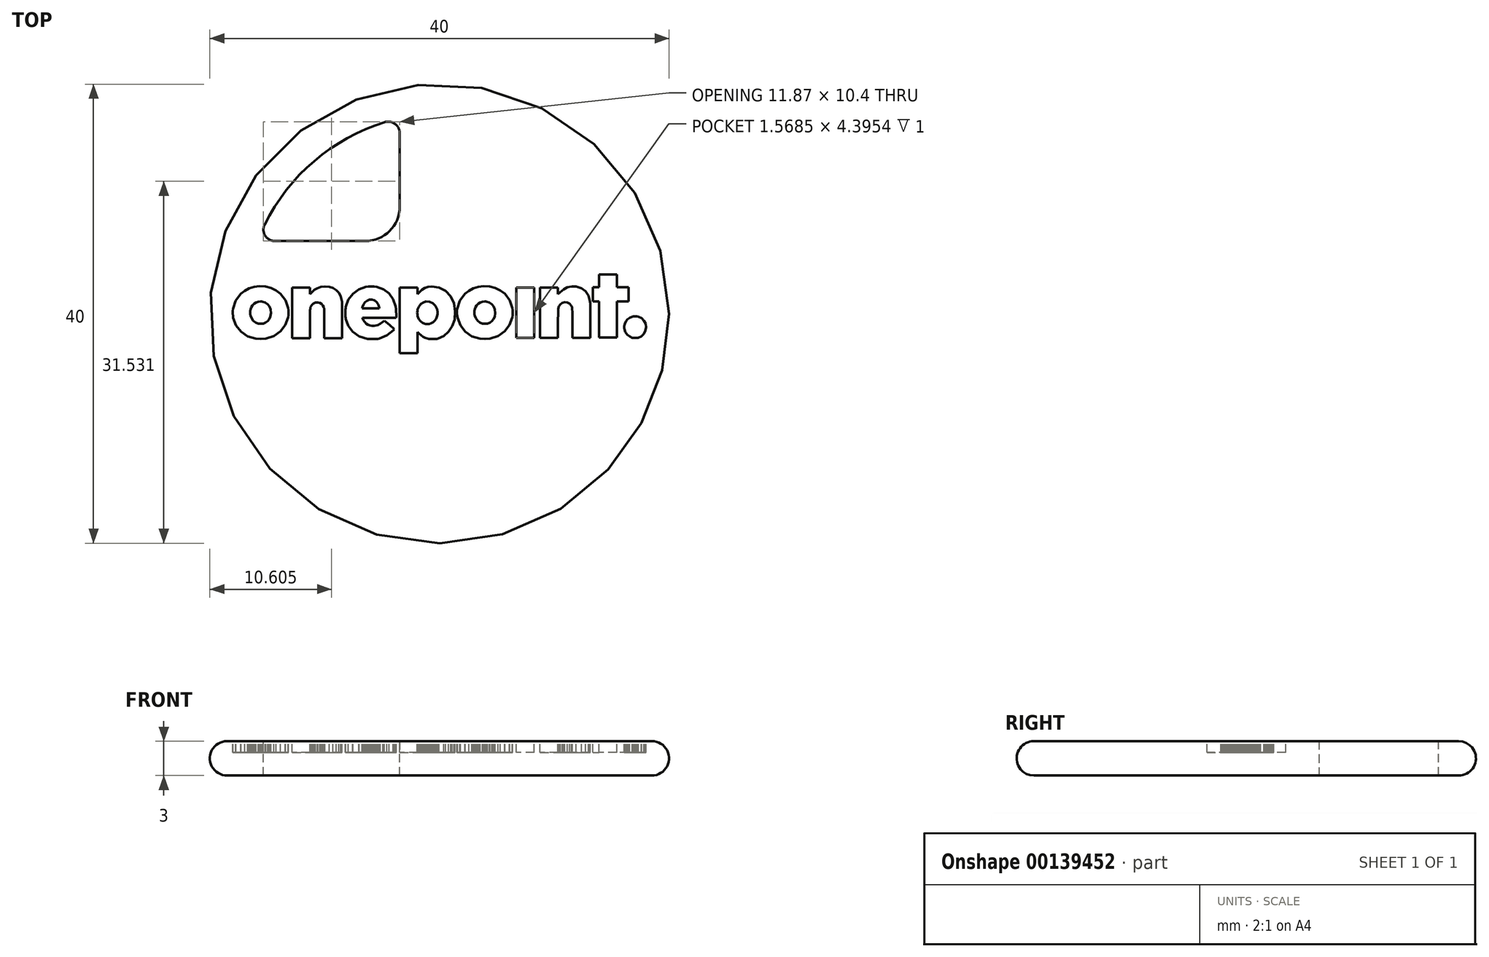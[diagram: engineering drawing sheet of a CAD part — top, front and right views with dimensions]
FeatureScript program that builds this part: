
annotation { "Feature Type Name" : "Feature", "Feature Type Description" : "" }
export const myFeature = defineFeature(function(context is Context, id is Id, definition is map)
    precondition{}
    {
        {
            var Q0;
            Q0=qCreatedBy(makeId("Top.planeOp"),FACE);
            var sketch = newSketch(context, id + "F0", { "sketchPlane" : qUnion([Q0])});
            skCircle(sketch, "E0", {"center": v(0, 0) * mm, "radius": 20 * mm});
            skSolve(sketch);
        }
        {
            var Q0;
            Q0 = qSketchRegion(id + "F0", true);
            var Q1;
            Q1=sQuery(id+"F0.wireOp",EDGE,"E0");
            extrude(context, id + "F1", {"entities" : qUnion([Q0]), "surfaceEntities" : qUnion([Q1]), "depth" : 3 * mm});
        }
        {
            var Q0;
            Q0=makeQuery(id+"F1.opExtrude","CAP_FACE",FACE,{"disambiguationData":[OSD([sQuery(id+"F0.wireOp",EDGE,"E0")])],"isStart":false});
            var sketch = newSketch(context, id + "F2", { "sketchPlane" : qUnion([Q0])});
            skLineSegment(sketch, "E1", {"start": v(-16, -2.18) * mm, "end": v(-16.7, -1.96) * mm});
            skLineSegment(sketch, "E2", {"start": v(-16.7, -1.96) * mm, "end": v(-17.28, -1.58) * mm});
            skLineSegment(sketch, "E3", {"start": v(-17.28, -1.58) * mm, "end": v(-17.7, -1.04) * mm});
            skLineSegment(sketch, "E4", {"start": v(-17.7, -1.04) * mm, "end": v(-17.96, -0.37) * mm});
            skLineSegment(sketch, "E5", {"start": v(-17.96, -0.37) * mm, "end": v(-17.99, -0.2) * mm});
            skLineSegment(sketch, "E6", {"start": v(-17.99, -0.2) * mm, "end": v(-18, 0.02) * mm});
            skLineSegment(sketch, "E7", {"start": v(-18, 0.02) * mm, "end": v(-18, 0.24) * mm});
            skLineSegment(sketch, "E8", {"start": v(-18, 0.24) * mm, "end": v(-17.98, 0.43) * mm});
            skLineSegment(sketch, "E9", {"start": v(-17.98, 0.43) * mm, "end": v(-17.75, 1.13) * mm});
            skLineSegment(sketch, "E10", {"start": v(-17.75, 1.13) * mm, "end": v(-17.3, 1.72) * mm});
            skLineSegment(sketch, "E11", {"start": v(-17.3, 1.72) * mm, "end": v(-16.96, 2) * mm});
            skLineSegment(sketch, "E12", {"start": v(-16.96, 2) * mm, "end": v(-16.57, 2.2) * mm});
            skLineSegment(sketch, "E13", {"start": v(-16.57, 2.2) * mm, "end": v(-16.15, 2.33) * mm});
            skLineSegment(sketch, "E14", {"start": v(-16.15, 2.33) * mm, "end": v(-15.69, 2.4) * mm});
            skLineSegment(sketch, "E15", {"start": v(-15.69, 2.4) * mm, "end": v(-15.16, 2.37) * mm});
            skLineSegment(sketch, "E16", {"start": v(-15.16, 2.37) * mm, "end": v(-14.67, 2.24) * mm});
            skLineSegment(sketch, "E17", {"start": v(-14.67, 2.24) * mm, "end": v(-14.22, 2.03) * mm});
            skLineSegment(sketch, "E18", {"start": v(-14.22, 2.03) * mm, "end": v(-13.83, 1.72) * mm});
            skLineSegment(sketch, "E19", {"start": v(-13.83, 1.72) * mm, "end": v(-13.4, 1.16) * mm});
            skLineSegment(sketch, "E20", {"start": v(-13.4, 1.16) * mm, "end": v(-13.17, 0.5) * mm});
            skLineSegment(sketch, "E21", {"start": v(-13.17, 0.5) * mm, "end": v(-13.15, 0.3) * mm});
            skLineSegment(sketch, "E22", {"start": v(-13.15, 0.3) * mm, "end": v(-13.15, 0.09) * mm});
            skLineSegment(sketch, "E23", {"start": v(-13.15, 0.09) * mm, "end": v(-13.16, -0.13) * mm});
            skLineSegment(sketch, "E24", {"start": v(-13.16, -0.13) * mm, "end": v(-13.18, -0.32) * mm});
            skLineSegment(sketch, "E25", {"start": v(-13.18, -0.32) * mm, "end": v(-13.42, -1) * mm});
            skLineSegment(sketch, "E26", {"start": v(-13.42, -1) * mm, "end": v(-13.85, -1.54) * mm});
            skLineSegment(sketch, "E27", {"start": v(-13.85, -1.54) * mm, "end": v(-14.43, -1.94) * mm});
            skLineSegment(sketch, "E28", {"start": v(-14.43, -1.94) * mm, "end": v(-15.12, -2.17) * mm});
            skLineSegment(sketch, "E29", {"start": v(-15.12, -2.17) * mm, "end": v(-15.56, -2.2) * mm});
            skLineSegment(sketch, "E30", {"start": v(-15.56, -2.2) * mm, "end": v(-16, -2.18) * mm});
            skLineSegment(sketch, "E31", {"start": v(-16, -2.18) * mm, "end": v(-16, -2.18) * mm});
            skLineSegment(sketch, "E32", {"start": v(-15.34, -0.86) * mm, "end": v(-15.13, -0.77) * mm});
            skLineSegment(sketch, "E33", {"start": v(-15.13, -0.77) * mm, "end": v(-14.96, -0.65) * mm});
            skLineSegment(sketch, "E34", {"start": v(-14.96, -0.65) * mm, "end": v(-14.82, -0.47) * mm});
            skLineSegment(sketch, "E35", {"start": v(-14.82, -0.47) * mm, "end": v(-14.72, -0.26) * mm});
            skLineSegment(sketch, "E36", {"start": v(-14.72, -0.26) * mm, "end": v(-14.66, 0.07) * mm});
            skLineSegment(sketch, "E37", {"start": v(-14.66, 0.07) * mm, "end": v(-14.7, 0.38) * mm});
            skLineSegment(sketch, "E38", {"start": v(-14.7, 0.38) * mm, "end": v(-14.8, 0.62) * mm});
            skLineSegment(sketch, "E39", {"start": v(-14.8, 0.62) * mm, "end": v(-14.97, 0.82) * mm});
            skLineSegment(sketch, "E40", {"start": v(-14.97, 0.82) * mm, "end": v(-15.17, 0.97) * mm});
            skLineSegment(sketch, "E41", {"start": v(-15.17, 0.97) * mm, "end": v(-15.41, 1.05) * mm});
            skLineSegment(sketch, "E42", {"start": v(-15.41, 1.05) * mm, "end": v(-15.51, 1.08) * mm});
            skLineSegment(sketch, "E43", {"start": v(-15.51, 1.08) * mm, "end": v(-15.59, 1.08) * mm});
            skLineSegment(sketch, "E44", {"start": v(-15.59, 1.08) * mm, "end": v(-15.78, 1.05) * mm});
            skLineSegment(sketch, "E45", {"start": v(-15.78, 1.05) * mm, "end": v(-15.99, 0.98) * mm});
            skLineSegment(sketch, "E46", {"start": v(-15.99, 0.98) * mm, "end": v(-16.15, 0.87) * mm});
            skLineSegment(sketch, "E47", {"start": v(-16.15, 0.87) * mm, "end": v(-16.28, 0.73) * mm});
            skLineSegment(sketch, "E48", {"start": v(-16.28, 0.73) * mm, "end": v(-16.39, 0.56) * mm});
            skLineSegment(sketch, "E49", {"start": v(-16.39, 0.56) * mm, "end": v(-16.45, 0.37) * mm});
            skLineSegment(sketch, "E50", {"start": v(-16.45, 0.37) * mm, "end": v(-16.48, 0.25) * mm});
            skLineSegment(sketch, "E51", {"start": v(-16.48, 0.25) * mm, "end": v(-16.48, 0.1) * mm});
            skLineSegment(sketch, "E52", {"start": v(-16.48, 0.1) * mm, "end": v(-16.48, -0.04) * mm});
            skLineSegment(sketch, "E53", {"start": v(-16.48, -0.04) * mm, "end": v(-16.45, -0.15) * mm});
            skLineSegment(sketch, "E54", {"start": v(-16.45, -0.15) * mm, "end": v(-16.36, -0.4) * mm});
            skLineSegment(sketch, "E55", {"start": v(-16.36, -0.4) * mm, "end": v(-16.21, -0.6) * mm});
            skLineSegment(sketch, "E56", {"start": v(-16.21, -0.6) * mm, "end": v(-16.02, -0.76) * mm});
            skLineSegment(sketch, "E57", {"start": v(-16.02, -0.76) * mm, "end": v(-15.8, -0.86) * mm});
            skLineSegment(sketch, "E58", {"start": v(-15.8, -0.86) * mm, "end": v(-15.57, -0.88) * mm});
            skLineSegment(sketch, "E59", {"start": v(-15.57, -0.88) * mm, "end": v(-15.34, -0.86) * mm});
            skLineSegment(sketch, "E60", {"start": v(-15.34, -0.86) * mm, "end": v(-15.34, -0.86) * mm});
            skLineSegment(sketch, "E61", {"start": v(-12.83, 0.07) * mm, "end": v(-12.83, 2.27) * mm});
            skLineSegment(sketch, "E62", {"start": v(-12.83, 2.27) * mm, "end": v(-11.27, 2.27) * mm});
            skLineSegment(sketch, "E63", {"start": v(-11.27, 2.27) * mm, "end": v(-11.27, 1.7) * mm});
            skLineSegment(sketch, "E64", {"start": v(-11.27, 1.7) * mm, "end": v(-11.1, 1.87) * mm});
            skLineSegment(sketch, "E65", {"start": v(-11.1, 1.87) * mm, "end": v(-10.88, 2.08) * mm});
            skLineSegment(sketch, "E66", {"start": v(-10.88, 2.08) * mm, "end": v(-10.63, 2.22) * mm});
            skLineSegment(sketch, "E67", {"start": v(-10.63, 2.22) * mm, "end": v(-10.31, 2.33) * mm});
            skLineSegment(sketch, "E68", {"start": v(-10.31, 2.33) * mm, "end": v(-9.96, 2.37) * mm});
            skLineSegment(sketch, "E69", {"start": v(-9.96, 2.37) * mm, "end": v(-9.6, 2.34) * mm});
            skLineSegment(sketch, "E70", {"start": v(-9.6, 2.34) * mm, "end": v(-9.27, 2.23) * mm});
            skLineSegment(sketch, "E71", {"start": v(-9.27, 2.23) * mm, "end": v(-9, 2.06) * mm});
            skLineSegment(sketch, "E72", {"start": v(-9, 2.06) * mm, "end": v(-8.78, 1.83) * mm});
            skLineSegment(sketch, "E73", {"start": v(-8.78, 1.83) * mm, "end": v(-8.62, 1.54) * mm});
            skLineSegment(sketch, "E74", {"start": v(-8.62, 1.54) * mm, "end": v(-8.5, 1.18) * mm});
            skLineSegment(sketch, "E75", {"start": v(-8.5, 1.18) * mm, "end": v(-8.5, 1.13) * mm});
            skLineSegment(sketch, "E76", {"start": v(-8.5, 1.13) * mm, "end": v(-8.49, 1.06) * mm});
            skLineSegment(sketch, "E77", {"start": v(-8.49, 1.06) * mm, "end": v(-8.48, 0.95) * mm});
            skLineSegment(sketch, "E78", {"start": v(-8.48, 0.95) * mm, "end": v(-8.48, 0.8) * mm});
            skLineSegment(sketch, "E79", {"start": v(-8.48, 0.8) * mm, "end": v(-8.48, 0.59) * mm});
            skLineSegment(sketch, "E80", {"start": v(-8.48, 0.59) * mm, "end": v(-8.47, 0.3) * mm});
            skLineSegment(sketch, "E81", {"start": v(-8.47, 0.3) * mm, "end": v(-8.47, -0.07) * mm});
            skLineSegment(sketch, "E82", {"start": v(-8.47, -0.07) * mm, "end": v(-8.47, -0.54) * mm});
            skLineSegment(sketch, "E83", {"start": v(-8.47, -0.54) * mm, "end": v(-8.47, -2.13) * mm});
            skLineSegment(sketch, "E84", {"start": v(-8.47, -2.13) * mm, "end": v(-10.02, -2.13) * mm});
            skLineSegment(sketch, "E85", {"start": v(-10.02, -2.13) * mm, "end": v(-10.02, -0.85) * mm});
            skLineSegment(sketch, "E86", {"start": v(-10.02, -0.85) * mm, "end": v(-10.03, -0.43) * mm});
            skLineSegment(sketch, "E87", {"start": v(-10.03, -0.43) * mm, "end": v(-10.03, -0.1) * mm});
            skLineSegment(sketch, "E88", {"start": v(-10.03, -0.1) * mm, "end": v(-10.03, 0.13) * mm});
            skLineSegment(sketch, "E89", {"start": v(-10.03, 0.13) * mm, "end": v(-10.04, 0.29) * mm});
            skLineSegment(sketch, "E90", {"start": v(-10.04, 0.29) * mm, "end": v(-10.04, 0.4) * mm});
            skLineSegment(sketch, "E91", {"start": v(-10.04, 0.4) * mm, "end": v(-10.05, 0.46) * mm});
            skLineSegment(sketch, "E92", {"start": v(-10.05, 0.46) * mm, "end": v(-10.06, 0.5) * mm});
            skLineSegment(sketch, "E93", {"start": v(-10.06, 0.5) * mm, "end": v(-10.07, 0.55) * mm});
            skLineSegment(sketch, "E94", {"start": v(-10.07, 0.55) * mm, "end": v(-10.15, 0.72) * mm});
            skLineSegment(sketch, "E95", {"start": v(-10.15, 0.72) * mm, "end": v(-10.26, 0.86) * mm});
            skLineSegment(sketch, "E96", {"start": v(-10.26, 0.86) * mm, "end": v(-10.4, 0.94) * mm});
            skLineSegment(sketch, "E97", {"start": v(-10.4, 0.94) * mm, "end": v(-10.58, 0.98) * mm});
            skLineSegment(sketch, "E98", {"start": v(-10.58, 0.98) * mm, "end": v(-10.8, 0.97) * mm});
            skLineSegment(sketch, "E99", {"start": v(-10.8, 0.97) * mm, "end": v(-10.97, 0.89) * mm});
            skLineSegment(sketch, "E100", {"start": v(-10.97, 0.89) * mm, "end": v(-11.12, 0.75) * mm});
            skLineSegment(sketch, "E101", {"start": v(-11.12, 0.75) * mm, "end": v(-11.23, 0.57) * mm});
            skLineSegment(sketch, "E102", {"start": v(-11.23, 0.57) * mm, "end": v(-11.24, 0.53) * mm});
            skLineSegment(sketch, "E103", {"start": v(-11.24, 0.53) * mm, "end": v(-11.25, 0.5) * mm});
            skLineSegment(sketch, "E104", {"start": v(-11.25, 0.5) * mm, "end": v(-11.26, 0.42) * mm});
            skLineSegment(sketch, "E105", {"start": v(-11.26, 0.42) * mm, "end": v(-11.26, 0.32) * mm});
            skLineSegment(sketch, "E106", {"start": v(-11.26, 0.32) * mm, "end": v(-11.26, 0.15) * mm});
            skLineSegment(sketch, "E107", {"start": v(-11.26, 0.15) * mm, "end": v(-11.27, -0.08) * mm});
            skLineSegment(sketch, "E108", {"start": v(-11.27, -0.08) * mm, "end": v(-11.27, -0.4) * mm});
            skLineSegment(sketch, "E109", {"start": v(-11.27, -0.4) * mm, "end": v(-11.27, -0.83) * mm});
            skLineSegment(sketch, "E110", {"start": v(-11.27, -0.83) * mm, "end": v(-11.27, -2.13) * mm});
            skLineSegment(sketch, "E111", {"start": v(-11.27, -2.13) * mm, "end": v(-12.83, -2.13) * mm});
            skLineSegment(sketch, "E112", {"start": v(-12.83, -2.13) * mm, "end": v(-12.83, 0.07) * mm});
            skLineSegment(sketch, "E113", {"start": v(-12.83, 0.07) * mm, "end": v(-12.83, 0.07) * mm});
            skLineSegment(sketch, "E114", {"start": v(-6.25, -2.2) * mm, "end": v(-6.98, -1.98) * mm});
            skLineSegment(sketch, "E115", {"start": v(-6.98, -1.98) * mm, "end": v(-7.57, -1.56) * mm});
            skLineSegment(sketch, "E116", {"start": v(-7.57, -1.56) * mm, "end": v(-7.94, -1.06) * mm});
            skLineSegment(sketch, "E117", {"start": v(-7.94, -1.06) * mm, "end": v(-8.16, -0.45) * mm});
            skLineSegment(sketch, "E118", {"start": v(-8.16, -0.45) * mm, "end": v(-8.18, -0.35) * mm});
            skLineSegment(sketch, "E119", {"start": v(-8.18, -0.35) * mm, "end": v(-8.19, -0.25) * mm});
            skLineSegment(sketch, "E120", {"start": v(-8.19, -0.25) * mm, "end": v(-8.2, -0.12) * mm});
            skLineSegment(sketch, "E121", {"start": v(-8.2, -0.12) * mm, "end": v(-8.2, 0.06) * mm});
            skLineSegment(sketch, "E122", {"start": v(-8.2, 0.06) * mm, "end": v(-8.2, 0.25) * mm});
            skLineSegment(sketch, "E123", {"start": v(-8.2, 0.25) * mm, "end": v(-8.19, 0.38) * mm});
            skLineSegment(sketch, "E124", {"start": v(-8.19, 0.38) * mm, "end": v(-8.18, 0.48) * mm});
            skLineSegment(sketch, "E125", {"start": v(-8.18, 0.48) * mm, "end": v(-8.16, 0.58) * mm});
            skLineSegment(sketch, "E126", {"start": v(-8.16, 0.58) * mm, "end": v(-7.93, 1.22) * mm});
            skLineSegment(sketch, "E127", {"start": v(-7.93, 1.22) * mm, "end": v(-7.54, 1.74) * mm});
            skLineSegment(sketch, "E128", {"start": v(-7.54, 1.74) * mm, "end": v(-7.03, 2.13) * mm});
            skLineSegment(sketch, "E129", {"start": v(-7.03, 2.13) * mm, "end": v(-6.41, 2.34) * mm});
            skLineSegment(sketch, "E130", {"start": v(-6.41, 2.34) * mm, "end": v(-6.2, 2.37) * mm});
            skLineSegment(sketch, "E131", {"start": v(-6.2, 2.37) * mm, "end": v(-5.95, 2.37) * mm});
            skLineSegment(sketch, "E132", {"start": v(-5.95, 2.37) * mm, "end": v(-5.69, 2.36) * mm});
            skLineSegment(sketch, "E133", {"start": v(-5.69, 2.36) * mm, "end": v(-5.47, 2.33) * mm});
            skLineSegment(sketch, "E134", {"start": v(-5.47, 2.33) * mm, "end": v(-4.87, 2.12) * mm});
            skLineSegment(sketch, "E135", {"start": v(-4.87, 2.12) * mm, "end": v(-4.4, 1.75) * mm});
            skLineSegment(sketch, "E136", {"start": v(-4.4, 1.75) * mm, "end": v(-4.04, 1.25) * mm});
            skLineSegment(sketch, "E137", {"start": v(-4.04, 1.25) * mm, "end": v(-3.82, 0.6) * mm});
            skLineSegment(sketch, "E138", {"start": v(-3.82, 0.6) * mm, "end": v(-3.8, 0.41) * mm});
            skLineSegment(sketch, "E139", {"start": v(-3.8, 0.41) * mm, "end": v(-3.77, 0.17) * mm});
            skLineSegment(sketch, "E140", {"start": v(-3.77, 0.17) * mm, "end": v(-3.76, -0.06) * mm});
            skLineSegment(sketch, "E141", {"start": v(-3.76, -0.06) * mm, "end": v(-3.76, -0.23) * mm});
            skLineSegment(sketch, "E142", {"start": v(-3.76, -0.23) * mm, "end": v(-3.78, -0.36) * mm});
            skLineSegment(sketch, "E143", {"start": v(-3.78, -0.36) * mm, "end": v(-6.7, -0.36) * mm});
            skLineSegment(sketch, "E144", {"start": v(-6.7, -0.36) * mm, "end": v(-6.7, -0.4) * mm});
            skLineSegment(sketch, "E145", {"start": v(-6.7, -0.4) * mm, "end": v(-6.67, -0.46) * mm});
            skLineSegment(sketch, "E146", {"start": v(-6.67, -0.46) * mm, "end": v(-6.63, -0.56) * mm});
            skLineSegment(sketch, "E147", {"start": v(-6.63, -0.56) * mm, "end": v(-6.52, -0.72) * mm});
            skLineSegment(sketch, "E148", {"start": v(-6.52, -0.72) * mm, "end": v(-6.39, -0.86) * mm});
            skLineSegment(sketch, "E149", {"start": v(-6.39, -0.86) * mm, "end": v(-6.22, -0.96) * mm});
            skLineSegment(sketch, "E150", {"start": v(-6.22, -0.96) * mm, "end": v(-6.03, -1.03) * mm});
            skLineSegment(sketch, "E151", {"start": v(-6.03, -1.03) * mm, "end": v(-5.88, -1.05) * mm});
            skLineSegment(sketch, "E152", {"start": v(-5.88, -1.05) * mm, "end": v(-5.7, -1.05) * mm});
            skLineSegment(sketch, "E153", {"start": v(-5.7, -1.05) * mm, "end": v(-5.53, -1.03) * mm});
            skLineSegment(sketch, "E154", {"start": v(-5.53, -1.03) * mm, "end": v(-5.38, -1) * mm});
            skLineSegment(sketch, "E155", {"start": v(-5.38, -1) * mm, "end": v(-5.15, -0.88) * mm});
            skLineSegment(sketch, "E156", {"start": v(-5.15, -0.88) * mm, "end": v(-4.92, -0.71) * mm});
            skLineSegment(sketch, "E157", {"start": v(-4.92, -0.71) * mm, "end": v(-4.8, -0.6) * mm});
            skLineSegment(sketch, "E158", {"start": v(-4.8, -0.6) * mm, "end": v(-4.36, -0.97) * mm});
            skLineSegment(sketch, "E159", {"start": v(-4.36, -0.97) * mm, "end": v(-3.93, -1.33) * mm});
            skLineSegment(sketch, "E160", {"start": v(-3.93, -1.33) * mm, "end": v(-4, -1.42) * mm});
            skLineSegment(sketch, "E161", {"start": v(-4, -1.42) * mm, "end": v(-4.56, -1.9) * mm});
            skLineSegment(sketch, "E162", {"start": v(-4.56, -1.9) * mm, "end": v(-5.25, -2.17) * mm});
            skLineSegment(sketch, "E163", {"start": v(-5.25, -2.17) * mm, "end": v(-5.35, -2.19) * mm});
            skLineSegment(sketch, "E164", {"start": v(-5.35, -2.19) * mm, "end": v(-5.46, -2.2) * mm});
            skLineSegment(sketch, "E165", {"start": v(-5.46, -2.2) * mm, "end": v(-5.6, -2.2) * mm});
            skLineSegment(sketch, "E166", {"start": v(-5.6, -2.2) * mm, "end": v(-5.8, -2.2) * mm});
            skLineSegment(sketch, "E167", {"start": v(-5.8, -2.2) * mm, "end": v(-5.94, -2.21) * mm});
            skLineSegment(sketch, "E168", {"start": v(-5.94, -2.21) * mm, "end": v(-6.07, -2.21) * mm});
            skLineSegment(sketch, "E169", {"start": v(-6.07, -2.21) * mm, "end": v(-6.18, -2.2) * mm});
            skLineSegment(sketch, "E170", {"start": v(-6.18, -2.2) * mm, "end": v(-6.25, -2.2) * mm});
            skLineSegment(sketch, "E171", {"start": v(-6.25, -2.2) * mm, "end": v(-6.25, -2.2) * mm});
            skLineSegment(sketch, "E172", {"start": v(-5.23, 0.47) * mm, "end": v(-5.24, 0.54) * mm});
            skLineSegment(sketch, "E173", {"start": v(-5.24, 0.54) * mm, "end": v(-5.26, 0.63) * mm});
            skLineSegment(sketch, "E174", {"start": v(-5.26, 0.63) * mm, "end": v(-5.3, 0.74) * mm});
            skLineSegment(sketch, "E175", {"start": v(-5.3, 0.74) * mm, "end": v(-5.34, 0.83) * mm});
            skLineSegment(sketch, "E176", {"start": v(-5.34, 0.83) * mm, "end": v(-5.47, 1.02) * mm});
            skLineSegment(sketch, "E177", {"start": v(-5.47, 1.02) * mm, "end": v(-5.65, 1.15) * mm});
            skLineSegment(sketch, "E178", {"start": v(-5.65, 1.15) * mm, "end": v(-5.86, 1.22) * mm});
            skLineSegment(sketch, "E179", {"start": v(-5.86, 1.22) * mm, "end": v(-6.1, 1.22) * mm});
            skLineSegment(sketch, "E180", {"start": v(-6.1, 1.22) * mm, "end": v(-6.3, 1.14) * mm});
            skLineSegment(sketch, "E181", {"start": v(-6.3, 1.14) * mm, "end": v(-6.47, 1) * mm});
            skLineSegment(sketch, "E182", {"start": v(-6.47, 1) * mm, "end": v(-6.6, 0.82) * mm});
            skLineSegment(sketch, "E183", {"start": v(-6.6, 0.82) * mm, "end": v(-6.7, 0.58) * mm});
            skLineSegment(sketch, "E184", {"start": v(-6.7, 0.58) * mm, "end": v(-6.73, 0.45) * mm});
            skLineSegment(sketch, "E185", {"start": v(-6.73, 0.45) * mm, "end": v(-5.98, 0.45) * mm});
            skLineSegment(sketch, "E186", {"start": v(-5.98, 0.45) * mm, "end": v(-5.75, 0.45) * mm});
            skLineSegment(sketch, "E187", {"start": v(-5.75, 0.45) * mm, "end": v(-5.57, 0.45) * mm});
            skLineSegment(sketch, "E188", {"start": v(-5.57, 0.45) * mm, "end": v(-5.44, 0.46) * mm});
            skLineSegment(sketch, "E189", {"start": v(-5.44, 0.46) * mm, "end": v(-5.35, 0.46) * mm});
            skLineSegment(sketch, "E190", {"start": v(-5.35, 0.46) * mm, "end": v(-5.29, 0.46) * mm});
            skLineSegment(sketch, "E191", {"start": v(-5.29, 0.46) * mm, "end": v(-5.25, 0.46) * mm});
            skLineSegment(sketch, "E192", {"start": v(-5.25, 0.46) * mm, "end": v(-5.23, 0.47) * mm});
            skLineSegment(sketch, "E193", {"start": v(-5.23, 0.47) * mm, "end": v(-5.23, 0.47) * mm});
            skLineSegment(sketch, "E194", {"start": v(-3.46, -0.57) * mm, "end": v(-3.46, 2.28) * mm});
            skLineSegment(sketch, "E195", {"start": v(-3.46, 2.28) * mm, "end": v(-1.9, 2.28) * mm});
            skLineSegment(sketch, "E196", {"start": v(-1.9, 2.28) * mm, "end": v(-1.9, 1.71) * mm});
            skLineSegment(sketch, "E197", {"start": v(-1.9, 1.71) * mm, "end": v(-1.76, 1.87) * mm});
            skLineSegment(sketch, "E198", {"start": v(-1.76, 1.87) * mm, "end": v(-1.51, 2.08) * mm});
            skLineSegment(sketch, "E199", {"start": v(-1.51, 2.08) * mm, "end": v(-1.26, 2.24) * mm});
            skLineSegment(sketch, "E200", {"start": v(-1.26, 2.24) * mm, "end": v(-0.98, 2.33) * mm});
            skLineSegment(sketch, "E201", {"start": v(-0.98, 2.33) * mm, "end": v(-0.67, 2.37) * mm});
            skLineSegment(sketch, "E202", {"start": v(-0.67, 2.37) * mm, "end": v(-0.03, 2.3) * mm});
            skLineSegment(sketch, "E203", {"start": v(-0.03, 2.3) * mm, "end": v(0.53, 2) * mm});
            skLineSegment(sketch, "E204", {"start": v(0.53, 2) * mm, "end": v(0.97, 1.53) * mm});
            skLineSegment(sketch, "E205", {"start": v(0.97, 1.53) * mm, "end": v(1.26, 0.9) * mm});
            skLineSegment(sketch, "E206", {"start": v(1.26, 0.9) * mm, "end": v(1.37, 0.2) * mm});
            skLineSegment(sketch, "E207", {"start": v(1.37, 0.2) * mm, "end": v(1.32, -0.53) * mm});
            skLineSegment(sketch, "E208", {"start": v(1.32, -0.53) * mm, "end": v(1.12, -1.1) * mm});
            skLineSegment(sketch, "E209", {"start": v(1.12, -1.1) * mm, "end": v(0.8, -1.58) * mm});
            skLineSegment(sketch, "E210", {"start": v(0.8, -1.58) * mm, "end": v(0.39, -1.94) * mm});
            skLineSegment(sketch, "E211", {"start": v(0.39, -1.94) * mm, "end": v(-0.12, -2.17) * mm});
            skLineSegment(sketch, "E212", {"start": v(-0.12, -2.17) * mm, "end": v(-0.22, -2.2) * mm});
            skLineSegment(sketch, "E213", {"start": v(-0.22, -2.2) * mm, "end": v(-0.31, -2.2) * mm});
            skLineSegment(sketch, "E214", {"start": v(-0.31, -2.2) * mm, "end": v(-0.42, -2.2) * mm});
            skLineSegment(sketch, "E215", {"start": v(-0.42, -2.2) * mm, "end": v(-0.57, -2.2) * mm});
            skLineSegment(sketch, "E216", {"start": v(-0.57, -2.2) * mm, "end": v(-0.73, -2.2) * mm});
            skLineSegment(sketch, "E217", {"start": v(-0.73, -2.2) * mm, "end": v(-0.84, -2.2) * mm});
            skLineSegment(sketch, "E218", {"start": v(-0.84, -2.2) * mm, "end": v(-0.93, -2.2) * mm});
            skLineSegment(sketch, "E219", {"start": v(-0.93, -2.2) * mm, "end": v(-1.03, -2.17) * mm});
            skLineSegment(sketch, "E220", {"start": v(-1.03, -2.17) * mm, "end": v(-1.23, -2.1) * mm});
            skLineSegment(sketch, "E221", {"start": v(-1.23, -2.1) * mm, "end": v(-1.42, -2) * mm});
            skLineSegment(sketch, "E222", {"start": v(-1.42, -2) * mm, "end": v(-1.6, -1.88) * mm});
            skLineSegment(sketch, "E223", {"start": v(-1.6, -1.88) * mm, "end": v(-1.78, -1.72) * mm});
            skLineSegment(sketch, "E224", {"start": v(-1.78, -1.72) * mm, "end": v(-1.9, -1.6) * mm});
            skLineSegment(sketch, "E225", {"start": v(-1.9, -1.6) * mm, "end": v(-1.9, -3.43) * mm});
            skLineSegment(sketch, "E226", {"start": v(-1.9, -3.43) * mm, "end": v(-3.46, -3.43) * mm});
            skLineSegment(sketch, "E227", {"start": v(-3.46, -3.43) * mm, "end": v(-3.46, -0.57) * mm});
            skLineSegment(sketch, "E228", {"start": v(-3.46, -0.57) * mm, "end": v(-3.46, -0.57) * mm});
            skLineSegment(sketch, "E229", {"start": v(-0.9, -0.9) * mm, "end": v(-0.72, -0.85) * mm});
            skLineSegment(sketch, "E230", {"start": v(-0.72, -0.85) * mm, "end": v(-0.55, -0.75) * mm});
            skLineSegment(sketch, "E231", {"start": v(-0.55, -0.75) * mm, "end": v(-0.4, -0.61) * mm});
            skLineSegment(sketch, "E232", {"start": v(-0.4, -0.61) * mm, "end": v(-0.28, -0.45) * mm});
            skLineSegment(sketch, "E233", {"start": v(-0.28, -0.45) * mm, "end": v(-0.2, -0.26) * mm});
            skLineSegment(sketch, "E234", {"start": v(-0.2, -0.26) * mm, "end": v(-0.17, -0.05) * mm});
            skLineSegment(sketch, "E235", {"start": v(-0.17, -0.05) * mm, "end": v(-0.17, 0.16) * mm});
            skLineSegment(sketch, "E236", {"start": v(-0.17, 0.16) * mm, "end": v(-0.2, 0.37) * mm});
            skLineSegment(sketch, "E237", {"start": v(-0.2, 0.37) * mm, "end": v(-0.34, 0.68) * mm});
            skLineSegment(sketch, "E238", {"start": v(-0.34, 0.68) * mm, "end": v(-0.56, 0.91) * mm});
            skLineSegment(sketch, "E239", {"start": v(-0.56, 0.91) * mm, "end": v(-0.85, 1.05) * mm});
            skLineSegment(sketch, "E240", {"start": v(-0.85, 1.05) * mm, "end": v(-1.17, 1.06) * mm});
            skLineSegment(sketch, "E241", {"start": v(-1.17, 1.06) * mm, "end": v(-1.41, 0.98) * mm});
            skLineSegment(sketch, "E242", {"start": v(-1.41, 0.98) * mm, "end": v(-1.63, 0.83) * mm});
            skLineSegment(sketch, "E243", {"start": v(-1.63, 0.83) * mm, "end": v(-1.79, 0.62) * mm});
            skLineSegment(sketch, "E244", {"start": v(-1.79, 0.62) * mm, "end": v(-1.9, 0.36) * mm});
            skLineSegment(sketch, "E245", {"start": v(-1.9, 0.36) * mm, "end": v(-1.92, 0.24) * mm});
            skLineSegment(sketch, "E246", {"start": v(-1.92, 0.24) * mm, "end": v(-1.92, 0.08) * mm});
            skLineSegment(sketch, "E247", {"start": v(-1.92, 0.08) * mm, "end": v(-1.92, -0.07) * mm});
            skLineSegment(sketch, "E248", {"start": v(-1.92, -0.07) * mm, "end": v(-1.9, -0.2) * mm});
            skLineSegment(sketch, "E249", {"start": v(-1.9, -0.2) * mm, "end": v(-1.8, -0.45) * mm});
            skLineSegment(sketch, "E250", {"start": v(-1.8, -0.45) * mm, "end": v(-1.65, -0.66) * mm});
            skLineSegment(sketch, "E251", {"start": v(-1.65, -0.66) * mm, "end": v(-1.45, -0.8) * mm});
            skLineSegment(sketch, "E252", {"start": v(-1.45, -0.8) * mm, "end": v(-1.22, -0.9) * mm});
            skLineSegment(sketch, "E253", {"start": v(-1.22, -0.9) * mm, "end": v(-1.07, -0.91) * mm});
            skLineSegment(sketch, "E254", {"start": v(-1.07, -0.91) * mm, "end": v(-0.9, -0.9) * mm});
            skLineSegment(sketch, "E255", {"start": v(6.7, 0.08) * mm, "end": v(6.7, 2.28) * mm});
            skLineSegment(sketch, "E256", {"start": v(6.7, 2.28) * mm, "end": v(8.26, 2.28) * mm});
            skLineSegment(sketch, "E257", {"start": v(8.26, 2.28) * mm, "end": v(8.26, -2.12) * mm});
            skLineSegment(sketch, "E258", {"start": v(8.26, -2.12) * mm, "end": v(6.7, -2.12) * mm});
            skLineSegment(sketch, "E259", {"start": v(6.7, -2.12) * mm, "end": v(6.7, 0.08) * mm});
            skLineSegment(sketch, "E260", {"start": v(3.53, -2.18) * mm, "end": v(2.83, -1.96) * mm});
            skLineSegment(sketch, "E261", {"start": v(2.83, -1.96) * mm, "end": v(2.26, -1.58) * mm});
            skLineSegment(sketch, "E262", {"start": v(2.26, -1.58) * mm, "end": v(1.83, -1.04) * mm});
            skLineSegment(sketch, "E263", {"start": v(1.83, -1.04) * mm, "end": v(1.57, -0.37) * mm});
            skLineSegment(sketch, "E264", {"start": v(1.57, -0.37) * mm, "end": v(1.54, -0.2) * mm});
            skLineSegment(sketch, "E265", {"start": v(1.54, -0.2) * mm, "end": v(1.53, 0.02) * mm});
            skLineSegment(sketch, "E266", {"start": v(1.53, 0.02) * mm, "end": v(1.54, 0.24) * mm});
            skLineSegment(sketch, "E267", {"start": v(1.54, 0.24) * mm, "end": v(1.55, 0.43) * mm});
            skLineSegment(sketch, "E268", {"start": v(1.55, 0.43) * mm, "end": v(1.79, 1.13) * mm});
            skLineSegment(sketch, "E269", {"start": v(1.79, 1.13) * mm, "end": v(2.23, 1.72) * mm});
            skLineSegment(sketch, "E270", {"start": v(2.23, 1.72) * mm, "end": v(2.58, 2) * mm});
            skLineSegment(sketch, "E271", {"start": v(2.58, 2) * mm, "end": v(2.96, 2.2) * mm});
            skLineSegment(sketch, "E272", {"start": v(2.96, 2.2) * mm, "end": v(3.39, 2.33) * mm});
            skLineSegment(sketch, "E273", {"start": v(3.39, 2.33) * mm, "end": v(3.84, 2.4) * mm});
            skLineSegment(sketch, "E274", {"start": v(3.84, 2.4) * mm, "end": v(4.37, 2.37) * mm});
            skLineSegment(sketch, "E275", {"start": v(4.37, 2.37) * mm, "end": v(4.86, 2.24) * mm});
            skLineSegment(sketch, "E276", {"start": v(4.86, 2.24) * mm, "end": v(5.3, 2.03) * mm});
            skLineSegment(sketch, "E277", {"start": v(5.3, 2.03) * mm, "end": v(5.7, 1.72) * mm});
            skLineSegment(sketch, "E278", {"start": v(5.7, 1.72) * mm, "end": v(6.13, 1.16) * mm});
            skLineSegment(sketch, "E279", {"start": v(6.13, 1.16) * mm, "end": v(6.36, 0.5) * mm});
            skLineSegment(sketch, "E280", {"start": v(6.36, 0.5) * mm, "end": v(6.38, 0.3) * mm});
            skLineSegment(sketch, "E281", {"start": v(6.38, 0.3) * mm, "end": v(6.39, 0.09) * mm});
            skLineSegment(sketch, "E282", {"start": v(6.39, 0.09) * mm, "end": v(6.38, -0.13) * mm});
            skLineSegment(sketch, "E283", {"start": v(6.38, -0.13) * mm, "end": v(6.35, -0.32) * mm});
            skLineSegment(sketch, "E284", {"start": v(6.35, -0.32) * mm, "end": v(6.1, -1) * mm});
            skLineSegment(sketch, "E285", {"start": v(6.1, -1) * mm, "end": v(5.68, -1.54) * mm});
            skLineSegment(sketch, "E286", {"start": v(5.68, -1.54) * mm, "end": v(5.1, -1.94) * mm});
            skLineSegment(sketch, "E287", {"start": v(5.1, -1.94) * mm, "end": v(4.41, -2.17) * mm});
            skLineSegment(sketch, "E288", {"start": v(4.41, -2.17) * mm, "end": v(3.97, -2.2) * mm});
            skLineSegment(sketch, "E289", {"start": v(3.97, -2.2) * mm, "end": v(3.53, -2.18) * mm});
            skLineSegment(sketch, "E290", {"start": v(4.2, -0.86) * mm, "end": v(4.4, -0.77) * mm});
            skLineSegment(sketch, "E291", {"start": v(4.4, -0.77) * mm, "end": v(4.57, -0.65) * mm});
            skLineSegment(sketch, "E292", {"start": v(4.57, -0.65) * mm, "end": v(4.71, -0.47) * mm});
            skLineSegment(sketch, "E293", {"start": v(4.71, -0.47) * mm, "end": v(4.81, -0.26) * mm});
            skLineSegment(sketch, "E294", {"start": v(4.81, -0.26) * mm, "end": v(4.87, 0.07) * mm});
            skLineSegment(sketch, "E295", {"start": v(4.87, 0.07) * mm, "end": v(4.83, 0.38) * mm});
            skLineSegment(sketch, "E296", {"start": v(4.83, 0.38) * mm, "end": v(4.72, 0.62) * mm});
            skLineSegment(sketch, "E297", {"start": v(4.72, 0.62) * mm, "end": v(4.56, 0.82) * mm});
            skLineSegment(sketch, "E298", {"start": v(4.56, 0.82) * mm, "end": v(4.36, 0.97) * mm});
            skLineSegment(sketch, "E299", {"start": v(4.36, 0.97) * mm, "end": v(4.12, 1.05) * mm});
            skLineSegment(sketch, "E300", {"start": v(4.12, 1.05) * mm, "end": v(4.02, 1.08) * mm});
            skLineSegment(sketch, "E301", {"start": v(4.02, 1.08) * mm, "end": v(3.95, 1.08) * mm});
            skLineSegment(sketch, "E302", {"start": v(3.95, 1.08) * mm, "end": v(3.75, 1.05) * mm});
            skLineSegment(sketch, "E303", {"start": v(3.75, 1.05) * mm, "end": v(3.54, 0.98) * mm});
            skLineSegment(sketch, "E304", {"start": v(3.54, 0.98) * mm, "end": v(3.39, 0.87) * mm});
            skLineSegment(sketch, "E305", {"start": v(3.39, 0.87) * mm, "end": v(3.25, 0.73) * mm});
            skLineSegment(sketch, "E306", {"start": v(3.25, 0.73) * mm, "end": v(3.14, 0.56) * mm});
            skLineSegment(sketch, "E307", {"start": v(3.14, 0.56) * mm, "end": v(3.08, 0.37) * mm});
            skLineSegment(sketch, "E308", {"start": v(3.08, 0.37) * mm, "end": v(3.06, 0.25) * mm});
            skLineSegment(sketch, "E309", {"start": v(3.06, 0.25) * mm, "end": v(3.05, 0.1) * mm});
            skLineSegment(sketch, "E310", {"start": v(3.05, 0.1) * mm, "end": v(3.06, -0.04) * mm});
            skLineSegment(sketch, "E311", {"start": v(3.06, -0.04) * mm, "end": v(3.08, -0.15) * mm});
            skLineSegment(sketch, "E312", {"start": v(3.08, -0.15) * mm, "end": v(3.17, -0.4) * mm});
            skLineSegment(sketch, "E313", {"start": v(3.17, -0.4) * mm, "end": v(3.32, -0.6) * mm});
            skLineSegment(sketch, "E314", {"start": v(3.32, -0.6) * mm, "end": v(3.51, -0.76) * mm});
            skLineSegment(sketch, "E315", {"start": v(3.51, -0.76) * mm, "end": v(3.74, -0.86) * mm});
            skLineSegment(sketch, "E316", {"start": v(3.74, -0.86) * mm, "end": v(3.96, -0.88) * mm});
            skLineSegment(sketch, "E317", {"start": v(3.96, -0.88) * mm, "end": v(4.2, -0.86) * mm});
            skLineSegment(sketch, "E318", {"start": v(4.2, -0.86) * mm, "end": v(4.2, -0.86) * mm});
            skLineSegment(sketch, "E319", {"start": v(8.78, 0.08) * mm, "end": v(8.78, 2.28) * mm});
            skLineSegment(sketch, "E320", {"start": v(8.78, 2.28) * mm, "end": v(10.33, 2.28) * mm});
            skLineSegment(sketch, "E321", {"start": v(10.33, 2.28) * mm, "end": v(10.33, 1.7) * mm});
            skLineSegment(sketch, "E322", {"start": v(10.33, 1.7) * mm, "end": v(10.5, 1.86) * mm});
            skLineSegment(sketch, "E323", {"start": v(10.5, 1.86) * mm, "end": v(10.81, 2.13) * mm});
            skLineSegment(sketch, "E324", {"start": v(10.81, 2.13) * mm, "end": v(11.15, 2.3) * mm});
            skLineSegment(sketch, "E325", {"start": v(11.15, 2.3) * mm, "end": v(11.5, 2.38) * mm});
            skLineSegment(sketch, "E326", {"start": v(11.5, 2.38) * mm, "end": v(11.9, 2.36) * mm});
            skLineSegment(sketch, "E327", {"start": v(11.9, 2.36) * mm, "end": v(12.37, 2.22) * mm});
            skLineSegment(sketch, "E328", {"start": v(12.37, 2.22) * mm, "end": v(12.73, 1.95) * mm});
            skLineSegment(sketch, "E329", {"start": v(12.73, 1.95) * mm, "end": v(12.99, 1.56) * mm});
            skLineSegment(sketch, "E330", {"start": v(12.99, 1.56) * mm, "end": v(13.12, 1.06) * mm});
            skLineSegment(sketch, "E331", {"start": v(13.12, 1.06) * mm, "end": v(13.13, 0.9) * mm});
            skLineSegment(sketch, "E332", {"start": v(13.13, 0.9) * mm, "end": v(13.13, 0.54) * mm});
            skLineSegment(sketch, "E333", {"start": v(13.13, 0.54) * mm, "end": v(13.14, 0.03) * mm});
            skLineSegment(sketch, "E334", {"start": v(13.14, 0.03) * mm, "end": v(13.14, -0.59) * mm});
            skLineSegment(sketch, "E335", {"start": v(13.14, -0.59) * mm, "end": v(13.14, -2.12) * mm});
            skLineSegment(sketch, "E336", {"start": v(13.14, -2.12) * mm, "end": v(11.58, -2.12) * mm});
            skLineSegment(sketch, "E337", {"start": v(11.58, -2.12) * mm, "end": v(11.58, -0.87) * mm});
            skLineSegment(sketch, "E338", {"start": v(11.58, -0.87) * mm, "end": v(11.58, -0.42) * mm});
            skLineSegment(sketch, "E339", {"start": v(11.58, -0.42) * mm, "end": v(11.58, -0.07) * mm});
            skLineSegment(sketch, "E340", {"start": v(11.58, -0.07) * mm, "end": v(11.58, 0.18) * mm});
            skLineSegment(sketch, "E341", {"start": v(11.58, 0.18) * mm, "end": v(11.57, 0.36) * mm});
            skLineSegment(sketch, "E342", {"start": v(11.57, 0.36) * mm, "end": v(11.56, 0.48) * mm});
            skLineSegment(sketch, "E343", {"start": v(11.56, 0.48) * mm, "end": v(11.54, 0.57) * mm});
            skLineSegment(sketch, "E344", {"start": v(11.54, 0.57) * mm, "end": v(11.52, 0.63) * mm});
            skLineSegment(sketch, "E345", {"start": v(11.52, 0.63) * mm, "end": v(11.49, 0.7) * mm});
            skLineSegment(sketch, "E346", {"start": v(11.49, 0.7) * mm, "end": v(11.35, 0.87) * mm});
            skLineSegment(sketch, "E347", {"start": v(11.35, 0.87) * mm, "end": v(11.15, 0.97) * mm});
            skLineSegment(sketch, "E348", {"start": v(11.15, 0.97) * mm, "end": v(10.93, 1) * mm});
            skLineSegment(sketch, "E349", {"start": v(10.93, 1) * mm, "end": v(10.7, 0.94) * mm});
            skLineSegment(sketch, "E350", {"start": v(10.7, 0.94) * mm, "end": v(10.54, 0.82) * mm});
            skLineSegment(sketch, "E351", {"start": v(10.54, 0.82) * mm, "end": v(10.41, 0.65) * mm});
            skLineSegment(sketch, "E352", {"start": v(10.41, 0.65) * mm, "end": v(10.39, 0.59) * mm});
            skLineSegment(sketch, "E353", {"start": v(10.39, 0.59) * mm, "end": v(10.37, 0.52) * mm});
            skLineSegment(sketch, "E354", {"start": v(10.37, 0.52) * mm, "end": v(10.35, 0.43) * mm});
            skLineSegment(sketch, "E355", {"start": v(10.35, 0.43) * mm, "end": v(10.34, 0.3) * mm});
            skLineSegment(sketch, "E356", {"start": v(10.34, 0.3) * mm, "end": v(10.34, 0.13) * mm});
            skLineSegment(sketch, "E357", {"start": v(10.34, 0.13) * mm, "end": v(10.33, -0.12) * mm});
            skLineSegment(sketch, "E358", {"start": v(10.33, -0.12) * mm, "end": v(10.33, -0.45) * mm});
            skLineSegment(sketch, "E359", {"start": v(10.33, -0.45) * mm, "end": v(10.33, -0.89) * mm});
            skLineSegment(sketch, "E360", {"start": v(10.33, -0.89) * mm, "end": v(10.33, -2.12) * mm});
            skLineSegment(sketch, "E361", {"start": v(10.33, -2.12) * mm, "end": v(8.77, -2.12) * mm});
            skLineSegment(sketch, "E362", {"start": v(8.77, -2.12) * mm, "end": v(8.77, 0.08) * mm});
            skLineSegment(sketch, "E363", {"start": v(8.77, 0.08) * mm, "end": v(8.78, 0.08) * mm});
            skLineSegment(sketch, "E364", {"start": v(13.9, -0.52) * mm, "end": v(13.9, 1.06) * mm});
            skLineSegment(sketch, "E365", {"start": v(13.9, 1.06) * mm, "end": v(13.37, 1.06) * mm});
            skLineSegment(sketch, "E366", {"start": v(13.37, 1.06) * mm, "end": v(13.37, 2.31) * mm});
            skLineSegment(sketch, "E367", {"start": v(13.37, 2.31) * mm, "end": v(13.9, 2.31) * mm});
            skLineSegment(sketch, "E368", {"start": v(13.9, 2.31) * mm, "end": v(13.9, 3.43) * mm});
            skLineSegment(sketch, "E369", {"start": v(13.9, 3.43) * mm, "end": v(15.45, 3.43) * mm});
            skLineSegment(sketch, "E370", {"start": v(15.45, 3.43) * mm, "end": v(15.45, 2.31) * mm});
            skLineSegment(sketch, "E371", {"start": v(15.45, 2.31) * mm, "end": v(16.46, 2.31) * mm});
            skLineSegment(sketch, "E372", {"start": v(16.46, 2.31) * mm, "end": v(16.46, 1.06) * mm});
            skLineSegment(sketch, "E373", {"start": v(16.46, 1.06) * mm, "end": v(15.45, 1.06) * mm});
            skLineSegment(sketch, "E374", {"start": v(15.45, 1.06) * mm, "end": v(15.45, -2.08) * mm});
            skLineSegment(sketch, "E375", {"start": v(15.45, -2.08) * mm, "end": v(13.9, -2.08) * mm});
            skLineSegment(sketch, "E376", {"start": v(13.9, -2.08) * mm, "end": v(13.9, -0.52) * mm});
            skLineSegment(sketch, "E377", {"start": v(16.8, -2.1) * mm, "end": v(16.56, -1.99) * mm});
            skLineSegment(sketch, "E378", {"start": v(16.56, -1.99) * mm, "end": v(16.36, -1.82) * mm});
            skLineSegment(sketch, "E379", {"start": v(16.36, -1.82) * mm, "end": v(16.2, -1.6) * mm});
            skLineSegment(sketch, "E380", {"start": v(16.2, -1.6) * mm, "end": v(16.11, -1.36) * mm});
            skLineSegment(sketch, "E381", {"start": v(16.11, -1.36) * mm, "end": v(16.1, -1.24) * mm});
            skLineSegment(sketch, "E382", {"start": v(16.1, -1.24) * mm, "end": v(16.1, -1.1) * mm});
            skLineSegment(sketch, "E383", {"start": v(16.1, -1.1) * mm, "end": v(16.12, -0.97) * mm});
            skLineSegment(sketch, "E384", {"start": v(16.12, -0.97) * mm, "end": v(16.15, -0.86) * mm});
            skLineSegment(sketch, "E385", {"start": v(16.15, -0.86) * mm, "end": v(16.25, -0.66) * mm});
            skLineSegment(sketch, "E386", {"start": v(16.25, -0.66) * mm, "end": v(16.4, -0.49) * mm});
            skLineSegment(sketch, "E387", {"start": v(16.4, -0.49) * mm, "end": v(16.57, -0.35) * mm});
            skLineSegment(sketch, "E388", {"start": v(16.57, -0.35) * mm, "end": v(16.78, -0.26) * mm});
            skLineSegment(sketch, "E389", {"start": v(16.78, -0.26) * mm, "end": v(16.9, -0.23) * mm});
            skLineSegment(sketch, "E390", {"start": v(16.9, -0.23) * mm, "end": v(17.05, -0.23) * mm});
            skLineSegment(sketch, "E391", {"start": v(17.05, -0.23) * mm, "end": v(17.2, -0.23) * mm});
            skLineSegment(sketch, "E392", {"start": v(17.2, -0.23) * mm, "end": v(17.32, -0.26) * mm});
            skLineSegment(sketch, "E393", {"start": v(17.32, -0.26) * mm, "end": v(17.6, -0.4) * mm});
            skLineSegment(sketch, "E394", {"start": v(17.6, -0.4) * mm, "end": v(17.82, -0.61) * mm});
            skLineSegment(sketch, "E395", {"start": v(17.82, -0.61) * mm, "end": v(17.95, -0.87) * mm});
            skLineSegment(sketch, "E396", {"start": v(17.95, -0.87) * mm, "end": v(18, -1.18) * mm});
            skLineSegment(sketch, "E397", {"start": v(18, -1.18) * mm, "end": v(17.95, -1.48) * mm});
            skLineSegment(sketch, "E398", {"start": v(17.95, -1.48) * mm, "end": v(17.8, -1.76) * mm});
            skLineSegment(sketch, "E399", {"start": v(17.8, -1.76) * mm, "end": v(17.58, -1.97) * mm});
            skLineSegment(sketch, "E400", {"start": v(17.58, -1.97) * mm, "end": v(17.3, -2.1) * mm});
            skLineSegment(sketch, "E401", {"start": v(17.3, -2.1) * mm, "end": v(17.18, -2.11) * mm});
            skLineSegment(sketch, "E402", {"start": v(17.18, -2.11) * mm, "end": v(17.05, -2.12) * mm});
            skLineSegment(sketch, "E403", {"start": v(17.05, -2.12) * mm, "end": v(16.91, -2.11) * mm});
            skLineSegment(sketch, "E404", {"start": v(16.91, -2.11) * mm, "end": v(16.8, -2.1) * mm});
            skLineSegment(sketch, "E405", {"start": v(16.8, -2.1) * mm, "end": v(16.8, -2.1) * mm});
            skSolve(sketch);
        }
        {
            var Q0;
            Q0 = qSketchRegion(id + "F2", true);
            extrude(context, id + "F3", {"entities" : qUnion([Q0]), "operationType" : NewBodyOperationType.REMOVE, "oppositeDirection" : true, "depth" : 1 * mm});
        }
        {
            var Q0;
            {var subQ0=sQuery(id+"F0.wireOp",EDGE,"E0");Q0=makeQuery(id+"F3.boolean.opBoolean","SPLIT",FACE,{"disambiguationData":[TD([makeQuery(id+"F1.opExtrude","SWEPT_FACE",FACE,{"disambiguationData":[OSD([subQ0])]})])],"derivedFrom":makeQuery(id+"F1.opExtrude","CAP_FACE",FACE,{"disambiguationData":[OSD([subQ0])],"isStart":false})});}
            var sketch = newSketch(context, id + "F4", { "sketchPlane" : qUnion([Q0])});
            skArc(sketch, "E406", {"start": v(-3.46, 17.04) * mm, "mid": v(-11, 13.23) * mm, "end": v(-15.86, 6.33) * mm});
            skLineSegment(sketch, "E407", {"start": v(-15.86, 6.33) * mm, "end": v(-3.46, 6.33) * mm});
            skLineSegment(sketch, "E408", {"start": v(-3.46, 17.04) * mm, "end": v(-3.46, 6.33) * mm});
            skSolve(sketch);
        }
        {
            var Q0;
            Q0 = qSketchRegion(id + "F4", true);
            extrude(context, id + "F5", {"entities" : qUnion([Q0]), "operationType" : NewBodyOperationType.REMOVE, "endBound" : BoundingType.THROUGH_ALL, "oppositeDirection" : true, "depth" : 25 * mm});
        }
        {
            var Q0;
            Q0=makeQuery(id+"F5.boolean.opBoolean","COPY",EDGE,{"derivedFrom":makeQuery(id+"F5.opExtrude","SWEPT_EDGE",EDGE,{"disambiguationData":[OSD([sQuery(id+"F4.wireOp",EDGE,"E407"),sQuery(id+"F4.wireOp",EDGE,"E408")])]})});
            fillet(context, id + "F6", {"entities" : qUnion([Q0]), "radius" : 3 * mm, "tangentPropagation" : true, "allowEdgeOverflow" : false});
        }
        {
            var Q0;
            Q0=makeQuery(id+"F5.boolean.opBoolean","COPY",EDGE,{"derivedFrom":makeQuery(id+"F5.opExtrude","SWEPT_EDGE",EDGE,{"disambiguationData":[OSD([sQuery(id+"F4.wireOp",EDGE,"E406"),sQuery(id+"F4.wireOp",EDGE,"E408")])]})});
            var Q1;
            Q1=makeQuery(id+"F5.boolean.opBoolean","COPY",EDGE,{"derivedFrom":makeQuery(id+"F5.opExtrude","SWEPT_EDGE",EDGE,{"disambiguationData":[OSD([sQuery(id+"F4.wireOp",EDGE,"E406"),sQuery(id+"F4.wireOp",EDGE,"E407")])]})});
            fillet(context, id + "F7", {"entities" : qUnion([Q0, Q1]), "radius" : 1 * mm, "tangentPropagation" : true, "allowEdgeOverflow" : false});
        }
        {
            var Q0;
            Q0=makeQuery(id+"F1.opExtrude","CAP_EDGE",EDGE,{"disambiguationData":[OSD([sQuery(id+"F0.wireOp",EDGE,"E0")])],"isStart":false});
            var Q1;
            Q1=makeQuery(id+"F1.opExtrude","CAP_EDGE",EDGE,{"disambiguationData":[OSD([sQuery(id+"F0.wireOp",EDGE,"E0")])],"isStart":true});
            fillet(context, id + "F8", {"entities" : qUnion([Q0, Q1]), "radius" : 1.5 * mm, "tangentPropagation" : true, "allowEdgeOverflow" : false});
        }
    });
